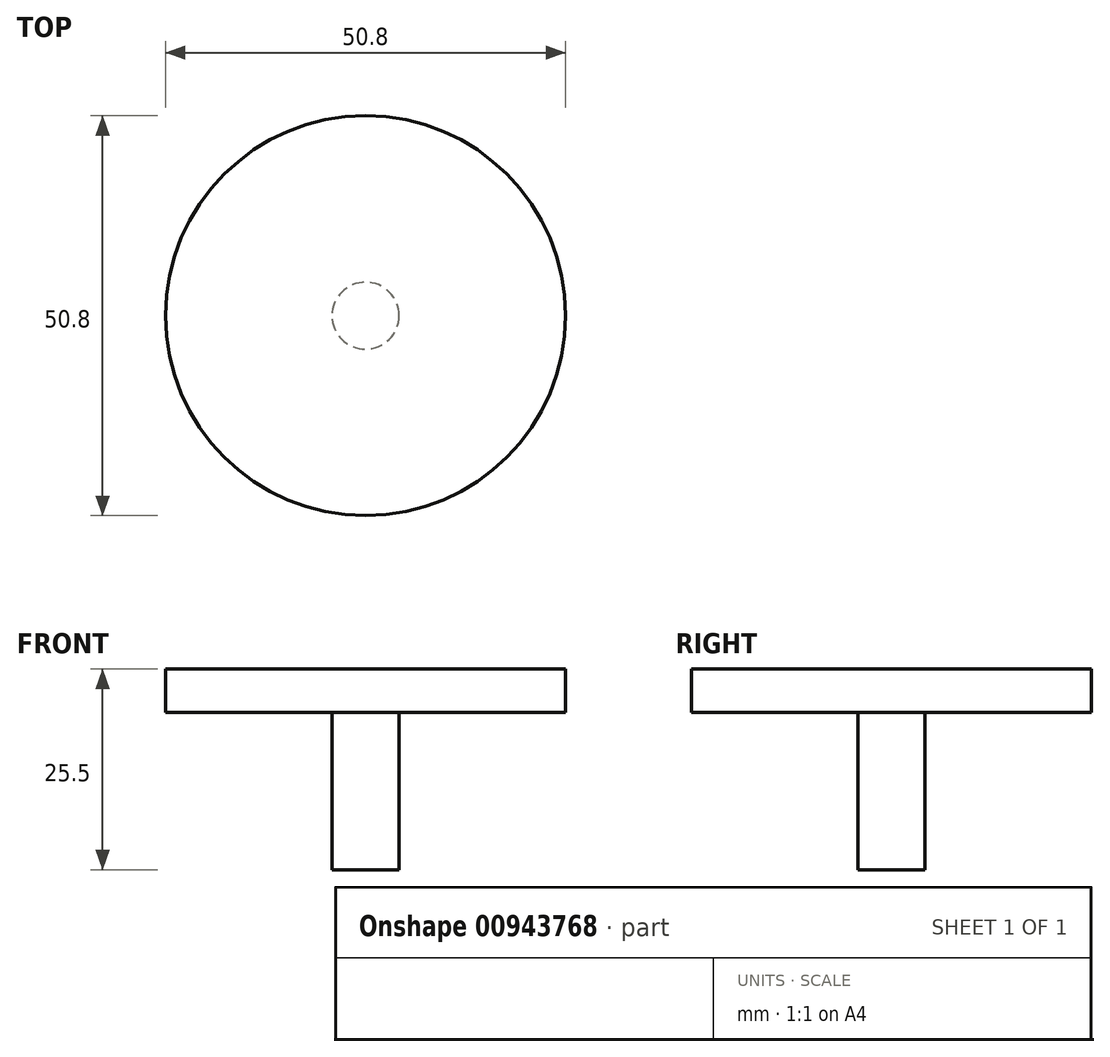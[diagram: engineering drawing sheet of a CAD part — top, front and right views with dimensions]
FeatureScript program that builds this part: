
annotation { "Feature Type Name" : "Feature", "Feature Type Description" : "" }
export const myFeature = defineFeature(function(context is Context, id is Id, definition is map)
    precondition{}
    {
        {
            var Q0;
            Q0=qCreatedBy(makeId("Front.planeOp"),FACE);
            var sketch = newSketch(context, id + "F0", { "sketchPlane" : qUnion([Q0])});
            skLineSegment(sketch, "E0.bottom", {"start": v(0, 0) * mm, "end": v(4.25, 0) * mm});
            skLineSegment(sketch, "E0.top", {"start": v(0, -20) * mm, "end": v(4.25, -20) * mm});
            skLineSegment(sketch, "E0.left", {"start": v(0, 0) * mm, "end": v(0, -20) * mm});
            skLineSegment(sketch, "E0.right", {"start": v(4.25, 0) * mm, "end": v(4.25, -20) * mm});
            skLineSegment(sketch, "E1.bottom", {"start": v(0, 0) * mm, "end": v(25.4, 0) * mm});
            skLineSegment(sketch, "E1.top", {"start": v(0, 5.5) * mm, "end": v(25.4, 5.5) * mm});
            skLineSegment(sketch, "E1.left", {"start": v(0, 0) * mm, "end": v(0, 5.5) * mm});
            skLineSegment(sketch, "E1.right", {"start": v(25.4, 0) * mm, "end": v(25.4, 5.5) * mm});
            skSolve(sketch);
        }
        {
            var Q0;
            Q0=makeQuery(id+"F0.imprint","IMPRINT",FACE,{"disambiguationData":[TD([[makeQuery(id+"F0.imprint","IMPRINT",EDGE,{"derivedFrom":sQuery(id+"F0.wireOp",EDGE,"E0.top")}),1.0]])]});
            var Q1;
            Q1=sQuery(id+"F0.wireOp",EDGE,"E0.left");
            revolve(context, id + "F1", {"surfaceOperationType" : NewSurfaceOperationType.NEW, "entities" : qUnion([Q0]), "axis" : qUnion([Q1]), "revolveType" : RevolveType.FULL});
        }
        {
            var Q0;
            Q0=makeQuery(id+"F0.imprint","IMPRINT",FACE,{"disambiguationData":[TD([[makeQuery(id+"F0.imprint","IMPRINT",EDGE,{"derivedFrom":sQuery(id+"F0.wireOp",EDGE,"E1.top")}),-1.0]])]});
            var Q1;
            Q1=sQuery(id+"F0.wireOp",EDGE,"E1.left");
            revolve(context, id + "F2", {"surfaceOperationType" : NewSurfaceOperationType.NEW, "entities" : qUnion([Q0]), "axis" : qUnion([Q1]), "revolveType" : RevolveType.FULL});
        }
    });
